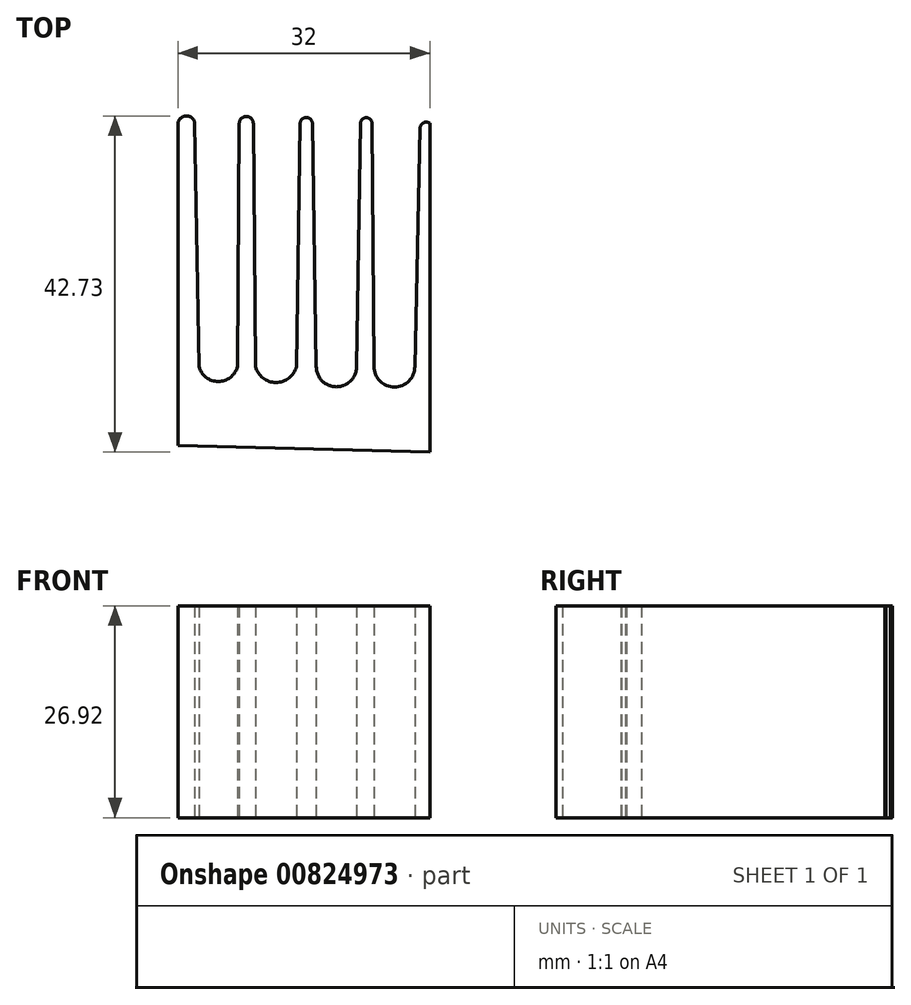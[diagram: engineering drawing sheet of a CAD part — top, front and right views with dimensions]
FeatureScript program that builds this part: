
annotation { "Feature Type Name" : "Feature", "Feature Type Description" : "" }
export const myFeature = defineFeature(function(context is Context, id is Id, definition is map)
    precondition{}
    {
        {
            var Q0;
            Q0=qCreatedBy(makeId("Top.planeOp"),FACE);
            var sketch = newSketch(context, id + "F0", { "sketchPlane" : qUnion([Q0])});
            skLineSegment(sketch, "E0", {"start": v(-13.37, 18.4) * mm, "end": v(-13.37, -22.58) * mm});
            skLineSegment(sketch, "E1", {"start": v(-13.37, -22.58) * mm, "end": v(18.63, -23.4) * mm});
            skLineSegment(sketch, "E2", {"start": v(18.63, -23.4) * mm, "end": v(18.63, 18.38) * mm});
            skLineSegment(sketch, "E3", {"start": v(17.4, 17.77) * mm, "end": v(16.72, -12.54) * mm});
            skLineSegment(sketch, "E4", {"start": v(11.55, -12.54) * mm, "end": v(11.28, 18.36) * mm});
            skLineSegment(sketch, "E5", {"start": v(9.82, 18.37) * mm, "end": v(9.32, -12.54) * mm});
            skLineSegment(sketch, "E6", {"start": v(4.2, -12.54) * mm, "end": v(3.7, 18.37) * mm});
            skLineSegment(sketch, "E7", {"start": v(2.16, 18.36) * mm, "end": v(1.66, -12.54) * mm});
            skLineSegment(sketch, "E8", {"start": v(-3.53, -12.54) * mm, "end": v(-3.8, 18.36) * mm});
            skLineSegment(sketch, "E9", {"start": v(-5.58, 18.4) * mm, "end": v(-5.82, -12.54) * mm});
            skLineSegment(sketch, "E10", {"start": v(-10.69, -12.54) * mm, "end": v(-11.24, 18.36) * mm});
            skArc(sketch, "E11", {"start": v(11.55, -12.54) * mm, "mid": v(14.13, -15.12) * mm, "end": v(16.72, -12.54) * mm});
            skArc(sketch, "E12", {"start": v(4.2, -12.54) * mm, "mid": v(6.76, -15.1) * mm, "end": v(9.32, -12.54) * mm});
            skArc(sketch, "E13", {"start": v(-3.53, -12.54) * mm, "mid": v(-0.93, -14.54) * mm, "end": v(1.66, -12.54) * mm});
            skArc(sketch, "E14", {"start": v(-10.69, -12.54) * mm, "mid": v(-8.25, -14.43) * mm, "end": v(-5.82, -12.54) * mm});
            skArc(sketch, "E15", {"start": v(18.63, 18.38) * mm, "mid": v(17.82, 18.45) * mm, "end": v(17.4, 17.77) * mm});
            skArc(sketch, "E16", {"start": v(11.28, 18.36) * mm, "mid": v(10.55, 19.09) * mm, "end": v(9.82, 18.37) * mm});
            skArc(sketch, "E17", {"start": v(3.7, 18.37) * mm, "mid": v(2.93, 19.13) * mm, "end": v(2.16, 18.36) * mm});
            skArc(sketch, "E18", {"start": v(-3.8, 18.36) * mm, "mid": v(-4.67, 19.25) * mm, "end": v(-5.58, 18.4) * mm});
            skArc(sketch, "E19", {"start": v(-11.24, 18.36) * mm, "mid": v(-12.3, 19.32) * mm, "end": v(-13.37, 18.4) * mm});
            skSolve(sketch);
        }
        {
            var Q0;
            Q0=makeQuery(id+"F0.imprint","IMPRINT",FACE,{"disambiguationData":[TD([[makeQuery(id+"F0.imprint","IMPRINT",EDGE,{"derivedFrom":sQuery(id+"F0.wireOp",EDGE,"E0")}),1.0]])]});
            extrude(context, id + "F1", {"entities" : qUnion([Q0]), "depth" : 26.92 * mm, "offsetDistance" : 25.4 * mm});
        }
    });
